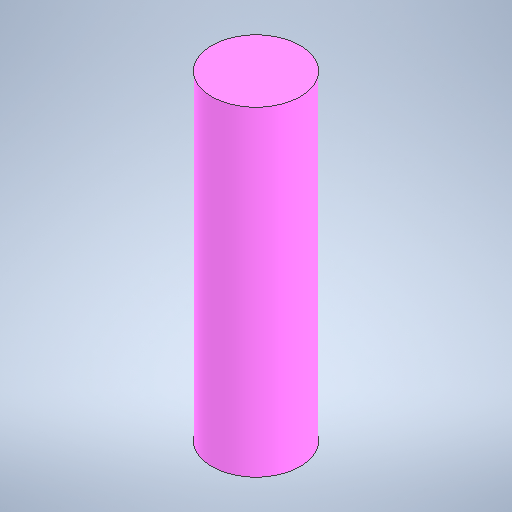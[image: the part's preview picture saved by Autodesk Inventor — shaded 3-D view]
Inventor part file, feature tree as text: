
AUTODESK INVENTOR PART (.ipt)
format: ipt  version: 2025.2 (Build 292293000, 293)  size: 237,568 bytes
history: native  units: mm
features: extrude x1, sketch x1
ambient origin geometry x8: Origin, YZ Plane, XZ Plane, XY Plane, X Axis, Y Axis, Z Axis, Center Point
bodies: Solid1 (feature_tree)
feature tree (2):
  extrude  "Extrusion1"  Depth=65.0mm TaperAngle=0.0deg
  sketch  "Sketch1"  dims[d0=18.0mm d10=65.0mm d11=0.0mm]
